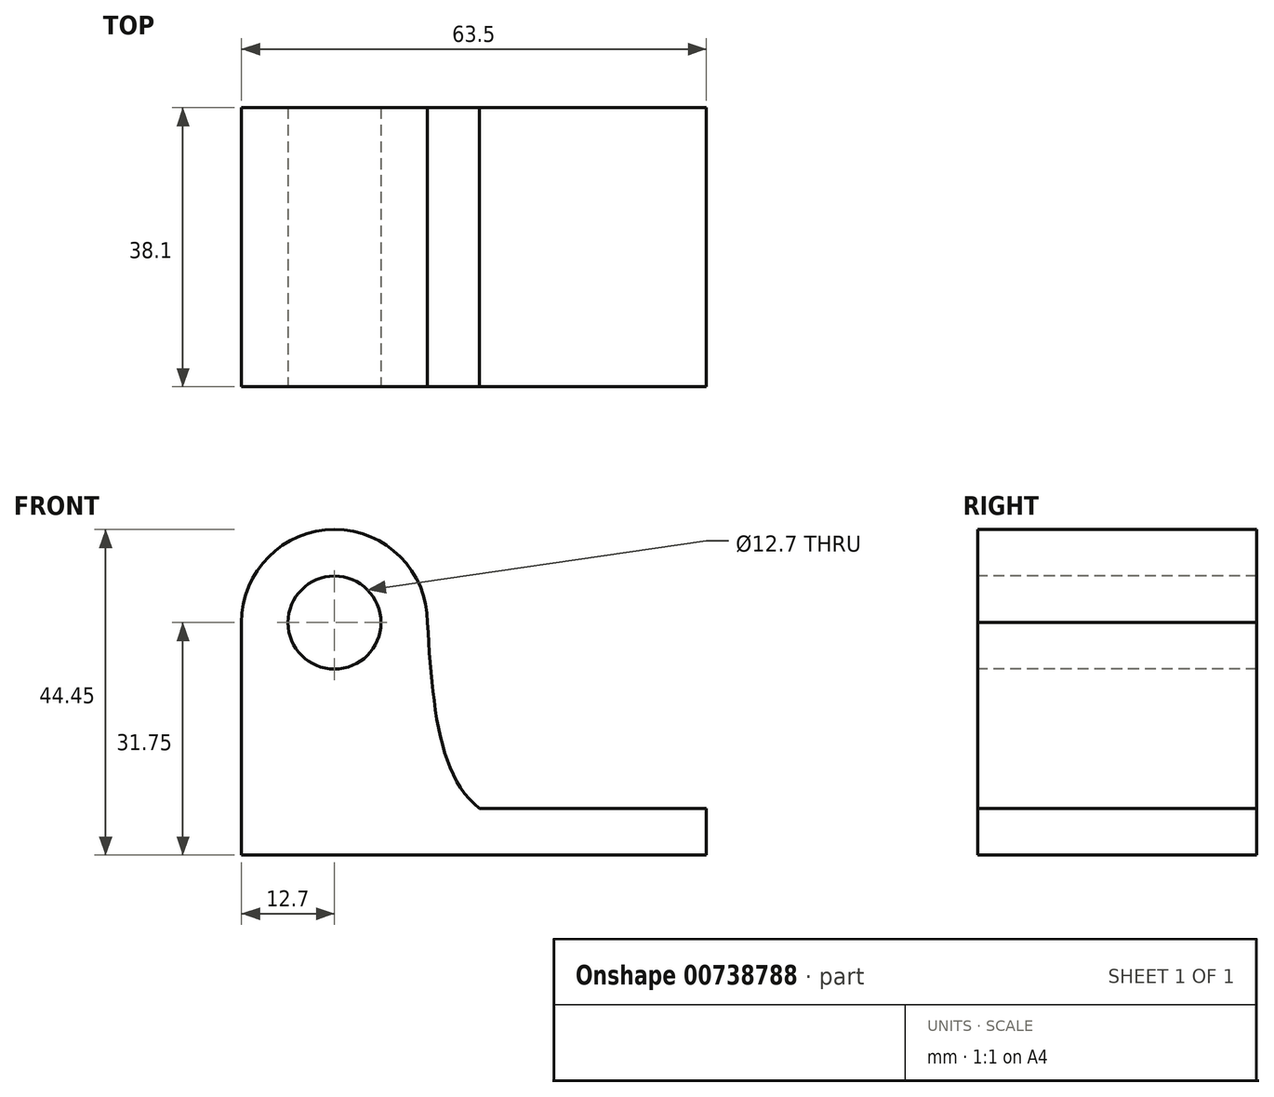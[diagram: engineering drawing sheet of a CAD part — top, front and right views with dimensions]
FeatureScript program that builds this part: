
annotation { "Feature Type Name" : "Feature", "Feature Type Description" : "" }
export const myFeature = defineFeature(function(context is Context, id is Id, definition is map)
    precondition{}
    {
        {
            var Q0;
            Q0=qCreatedBy(makeId("Front.planeOp"),FACE);
            var sketch = newSketch(context, id + "F0", { "sketchPlane" : qUnion([Q0])});
            skLineSegment(sketch, "E0", {"start": v(0, 0) * mm, "end": v(0, 44.45) * mm});
            skLineSegment(sketch, "E1", {"start": v(0, 44.45) * mm, "end": v(25.4, 44.45) * mm});
            skLineSegment(sketch, "E2", {"start": v(25.4, 44.45) * mm, "end": v(25.4, 6.35) * mm});
            skLineSegment(sketch, "E3", {"start": v(25.4, 6.35) * mm, "end": v(63.5, 6.35) * mm});
            skLineSegment(sketch, "E4", {"start": v(63.5, 6.35) * mm, "end": v(63.5, 0) * mm});
            skLineSegment(sketch, "E5", {"start": v(63.5, 0) * mm, "end": v(0, 0) * mm});
            skSolve(sketch);
        }
        {
            var Q0;
            Q0 = qSketchRegion(id + "F0", true);
            extrude(context, id + "F1", {"entities" : qUnion([Q0]), "depth" : 38.1 * mm, "offsetDistance" : 25.4 * mm});
        }
        {
            var Q0;
            Q0=makeQuery(id+"F1.opExtrude","CAP_FACE",FACE,{"disambiguationData":[OSD([sQuery(id+"F0.wireOp",EDGE,"E0"),sQuery(id+"F0.wireOp",EDGE,"E1"),sQuery(id+"F0.wireOp",EDGE,"E2"),sQuery(id+"F0.wireOp",EDGE,"E3"),sQuery(id+"F0.wireOp",EDGE,"E4"),sQuery(id+"F0.wireOp",EDGE,"E5")])],"isStart":false});
            var sketch = newSketch(context, id + "F2", { "sketchPlane" : qUnion([Q0])});
            skLineSegment(sketch, "E6", {"start": v(12.7, 44.45) * mm, "end": v(12.7, 0) * mm});
            skLineSegment(sketch, "E7", {"start": v(25.4, 44.45) * mm, "end": v(25.4, 31.75) * mm});
            skLineSegment(sketch, "E8", {"start": v(25.4, 31.75) * mm, "end": v(0, 31.75) * mm});
            skCircle(sketch, "E9", {"center": v(12.7, 31.75) * mm, "radius": 12.7 * mm});
            skCircle(sketch, "E10", {"center": v(12.7, 31.75) * mm, "radius": 6.35 * mm});
            skSolve(sketch);
        }
        {
            var Q0;
            {var subQ0=sQuery(id+"F2.wireOp",EDGE,"E10");var subQ1=sQuery(id+"F2.wireOp",EDGE,"E6");var subQ2=makeQuery(id+"F2.imprint","INTERSECT",VERTEX,{"disambiguationData":[OD(0.0)],"derivedFrom":[subQ1,subQ0]});Q0=makeQuery(id+"F2.imprint","IMPRINT",FACE,{"disambiguationData":[TD([[makeQuery(id+"F2.imprint","IMPRINT",EDGE,{"disambiguationData":[TD([[subQ2,-1.0]])],"derivedFrom":subQ1}),-1.0]])]});}
            var Q1;
            {var subQ0=sQuery(id+"F2.wireOp",EDGE,"E10");var subQ1=sQuery(id+"F2.wireOp",EDGE,"E6");var subQ2=makeQuery(id+"F2.imprint","INTERSECT",VERTEX,{"disambiguationData":[OD(0.0)],"derivedFrom":[subQ1,subQ0]});Q1=makeQuery(id+"F2.imprint","IMPRINT",FACE,{"disambiguationData":[TD([[makeQuery(id+"F2.imprint","IMPRINT",EDGE,{"disambiguationData":[TD([[subQ2,-1.0]])],"derivedFrom":subQ1}),1.0]])]});}
            var Q2;
            {var subQ0=sQuery(id+"F2.wireOp",EDGE,"E8");var subQ1=sQuery(id+"F2.wireOp",EDGE,"E6");var subQ2=makeQuery(id+"F2.imprint","INTERSECT",VERTEX,{"derivedFrom":[subQ1,subQ0]});Q2=makeQuery(id+"F2.imprint","IMPRINT",FACE,{"disambiguationData":[TD([[makeQuery(id+"F2.imprint","IMPRINT",EDGE,{"disambiguationData":[TD([[subQ2,-1.0]])],"derivedFrom":subQ1}),1.0]])]});}
            var Q3;
            {var subQ0=sQuery(id+"F2.wireOp",EDGE,"E8");var subQ1=sQuery(id+"F2.wireOp",EDGE,"E6");var subQ2=makeQuery(id+"F2.imprint","INTERSECT",VERTEX,{"derivedFrom":[subQ1,subQ0]});Q3=makeQuery(id+"F2.imprint","IMPRINT",FACE,{"disambiguationData":[TD([[makeQuery(id+"F2.imprint","IMPRINT",EDGE,{"disambiguationData":[TD([[subQ2,-1.0]])],"derivedFrom":subQ1}),-1.0]])]});}
            var Q4;
            {var subQ0=sQuery(id+"F2.wireOp",EDGE,"E7");Q4=makeQuery(id+"F2.imprint","IMPRINT",FACE,{"disambiguationData":[TD([[makeQuery(id+"F2.imprint","IMPRINT",EDGE,{"derivedFrom":subQ0}),-1.0]])]});}
            var Q5;
            {var subQ1=makeQuery(id+"F1.opExtrude","CAP_EDGE",EDGE,{"disambiguationData":[OSD([sQuery(id+"F0.wireOp",EDGE,"E1")])],"isStart":false});var subQ3=makeQuery(id+"F1.opExtrude","CAP_EDGE",EDGE,{"disambiguationData":[OSD([sQuery(id+"F0.wireOp",EDGE,"E0")])],"isStart":false});var subQ5=makeQuery(id+"F2.imprint","INTERSECT",VERTEX,{"derivedFrom":[subQ3,subQ1]});Q5=makeQuery(id+"F2.imprint","IMPRINT",FACE,{"disambiguationData":[TD([[makeQuery(id+"F2.imprint","IMPRINT",EDGE,{"disambiguationData":[TD([[subQ5,1.0]])],"derivedFrom":subQ3}),-1.0]])]});}
            extrude(context, id + "F3", {"entities" : qUnion([Q0, Q1, Q2, Q3, Q4, Q5]), "operationType" : NewBodyOperationType.REMOVE, "endBound" : BoundingType.THROUGH_ALL, "oppositeDirection" : true, "depth" : 25.4 * mm, "offsetDistance" : 25.4 * mm});
        }
        {
            var Q0;
            Q0=makeQuery(id+"F1.opExtrude","CAP_FACE",FACE,{"disambiguationData":[OSD([sQuery(id+"F0.wireOp",EDGE,"E0"),sQuery(id+"F0.wireOp",EDGE,"E1"),sQuery(id+"F0.wireOp",EDGE,"E2"),sQuery(id+"F0.wireOp",EDGE,"E3"),sQuery(id+"F0.wireOp",EDGE,"E4"),sQuery(id+"F0.wireOp",EDGE,"E5")])],"isStart":false});
            var sketch = newSketch(context, id + "F4", { "sketchPlane" : qUnion([Q0])});
            skFitSpline(sketch, "E11", {"points": [v(25.4, 31.75) * mm, v(32.55, 6.35) * mm, v(63.5, 6.35) * mm], "startDerivative": vector(4.17, -65.61) * mm, "endDerivative": vector(71.14, 13.76) * mm});
            skSolve(sketch);
        }
        {
            var Q0;
            Q0 = qSketchRegion(id + "F4", true);
            var Q1;
            {var subQ1=makeQuery(id+"F1.opExtrude","CAP_EDGE",EDGE,{"disambiguationData":[OSD([sQuery(id+"F0.wireOp",EDGE,"E2")])],"isStart":false});var subQ2=subQ1;Q1=makeQuery(id+"F4.imprint","IMPRINT",FACE,{"disambiguationData":[TD([[makeQuery(id+"F4.imprint","IMPRINT",EDGE,{"derivedFrom":subQ2}),1.0]])]});}
            extrude(context, id + "F5", {"entities" : qUnion([Q0, Q1]), "operationType" : NewBodyOperationType.ADD, "oppositeDirection" : true, "depth" : 38.1 * mm, "offsetDistance" : 25.4 * mm});
        }
        {
            var Q0;
            Q0=qCreatedBy(makeId("Front.planeOp"),FACE);
            var sketch = newSketch(context, id + "F6", { "sketchPlane" : qUnion([Q0])});
            skLineSegment(sketch, "E12", {"start": v(63.5, 6.4) * mm, "end": v(0, 6.4) * mm});
            skLineSegment(sketch, "E13", {"start": v(0, 6.4) * mm, "end": v(0, 0) * mm});
            skLineSegment(sketch, "E14", {"start": v(0, 0) * mm, "end": v(63.5, 0) * mm});
            skLineSegment(sketch, "E15", {"start": v(63.5, 0) * mm, "end": v(63.5, 6.4) * mm});
            skSolve(sketch);
        }
        {
            var Q0;
            Q0=makeQuery(id+"F6.imprint","IMPRINT",FACE,{"disambiguationData":[TD([[makeQuery(id+"F6.imprint","IMPRINT",EDGE,{"derivedFrom":sQuery(id+"F6.wireOp",EDGE,"E12")}),1.0]])]});
            extrude(context, id + "F7", {"entities" : qUnion([Q0]), "operationType" : NewBodyOperationType.ADD, "depth" : 38.1 * mm, "offsetDistance" : 25.4 * mm});
        }
    });
